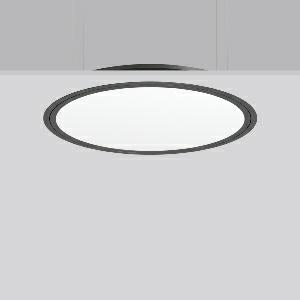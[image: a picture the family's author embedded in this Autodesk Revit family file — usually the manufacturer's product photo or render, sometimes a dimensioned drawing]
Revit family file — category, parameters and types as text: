
# Revit family: triona_round_e_312383_0031_12_d9f4
name_source: partatom
category: Lighting Fixtures
units: mm (PartAtom-declared; Revit-internal decimal feet)

## family parameters
Cut with Voids When Loaded = No
Host = Face
Light Source = No
Part Type = Normal
Room Calculation Point = No
Round Connector Dimension = Use Diameter
Shared = No

## types (1)
- TRIONA round E (1 x LED Modul 830, 6450 lm, 3000)
    Apparent Load = 70 VA
    CIE Flux Codes = 49 80 96 100 100
    Color Rendering = 80
    Color Temperature = 3000
    Default Elevation = 1800 mm
    Description = Series: TRIONA round
Decorative round LED recessed surface luminaire. Cover made of sheet steel, powder-coated. Frame made of aluminium, powder-coated. Recessed ring: aluminium extrusion profile, powder coated. Light emission through a diffuser: plastic, opal. Lightguide and diffuser made of non-yellowing plastic (PMMA). Lateral light emission (RZB SIDELITE technology) for above-average homogeneous light distribution. Suitable for installation in cavity ceilings. Tool-free mounting system thanks to the rocker arm mechanism (patent pending). Electronic ballast included. Very easy installation thanks to Plug+Play connection. 
Colour: anthracite metallic (DB703)
Diameter: 725 mm
Height: 2 mm
Cut-out diameter: 702 mm
Recess height: 100 mm
Luminaire: recess height: 89 mm
Lamp: LED
Socket: without socket
Colour temperature: 3000K
Colour rendering index (CRI): 80
System power: 70 W
Rated luminous flux: 6450 lm
Luminous efficiency: 92 lm/W
Control gear: Converter, dimmable, DALI
Protection class: I
Type of protection: IP 40
    Height = 0 mm  [stored 0 ft]
    Lamp = 1 x LED Modul 830
    Lamp Light Flux = 6450 lm
    Lamp count = 1
    Length = 725 mm
    Lifetime = 50000 h
    Luminous efficacy = 92 lm/W
    Manufacturer = RZB
    ModVariant = No
    Model = 312383.0031.12
    Mounting Place = Ceiling
    Mounting Type = Recessed
    Number of Poles = 1
    OnlyDefault = Yes
    Power Factor = 1
    Product Name = TRIONA round E
    Product group = Recessed modular luminaires
    ProductGroupID = 406
    Protection Class = Protection class I
    Protection Degree = IP 20
    RLX_Detail_Level = 1
    RLX_Emergency_Light_Flux = 0 lm
    RLX_Emergency_Type = 0
    RLX_Emergency_Type_DB = No
    RlxData = <blob elided: 39333 chars, md5=774e089e>
    Socket = socket
    Standby Power = 0 W
    System Light Flux = 6450 lm
    System Power = 70 W
    Type Comments = Product without accessories
    Type Image = 312383.0031.12.jpg
    URL = http://relux.com
    VarID = ---
    Voltage = 230 V
    Voltage Range = 220-240 V
    Weight = 0.00 kg
    Width = 0 mm  [stored 0 ft]

note: [stored X ft] marks values corroborated as IEEE doubles in the binary element streams (Revit-internal decimal feet)

## geometry (parser evidence)
native form markers: Blend x4, Sweep x11
no freeform markers — native parametric forms only
